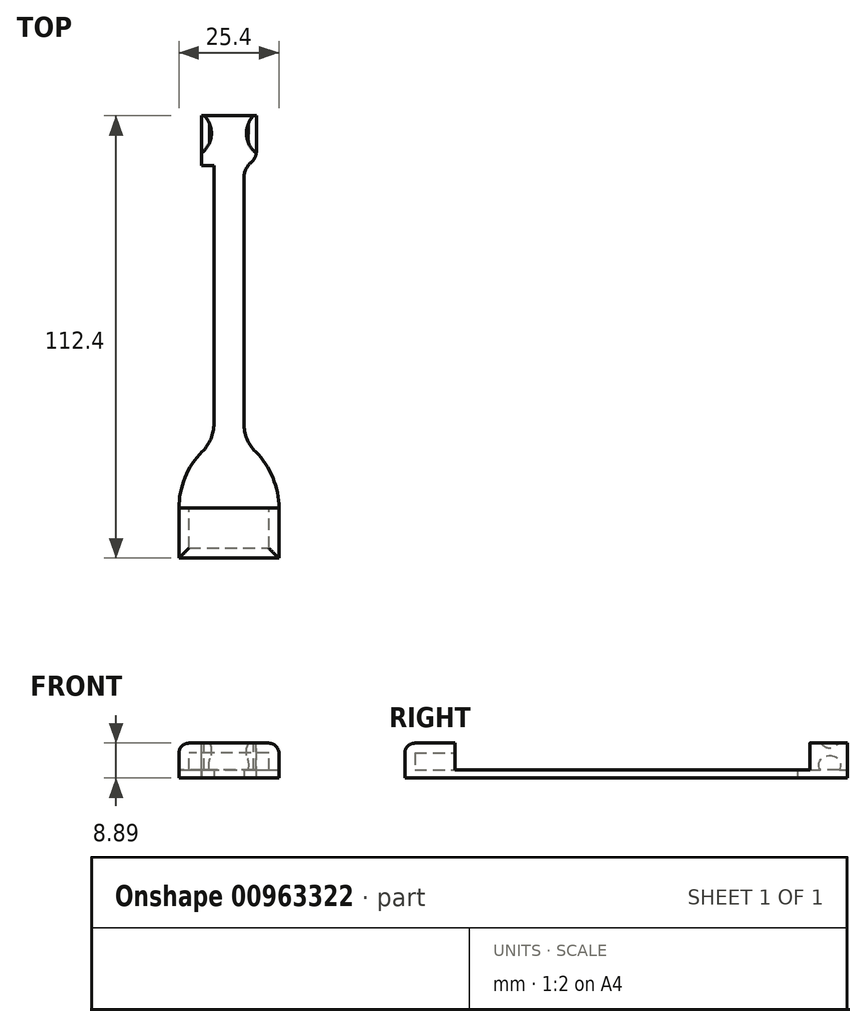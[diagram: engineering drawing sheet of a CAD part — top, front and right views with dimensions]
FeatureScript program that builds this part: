
annotation { "Feature Type Name" : "Feature", "Feature Type Description" : "" }
export const myFeature = defineFeature(function(context is Context, id is Id, definition is map)
    precondition{}
    {
        {
            var Q0;
            Q0=qCreatedBy(makeId("Top.planeOp"),FACE);
            var sketch = newSketch(context, id + "F0", { "sketchPlane" : qUnion([Q0])});
            skLineSegment(sketch, "E0.bottom", {"start": v(0, 0) * mm, "end": v(25.4, 0) * mm});
            skLineSegment(sketch, "E0.top", {"start": v(0, 12.7) * mm, "end": v(25.4, 12.7) * mm});
            skLineSegment(sketch, "E0.left", {"start": v(0, 0) * mm, "end": v(0, 12.7) * mm});
            skLineSegment(sketch, "E0.right", {"start": v(25.4, 0) * mm, "end": v(25.4, 12.7) * mm});
            skSolve(sketch);
        }
        {
            var Q0;
            Q0=makeQuery(id+"F0.imprint","IMPRINT",FACE,{"disambiguationData":[TD([[makeQuery(id+"F0.imprint","IMPRINT",EDGE,{"derivedFrom":sQuery(id+"F0.wireOp",EDGE,"E0.bottom")}),1.0]])]});
            var Q1;
            {var subQ0=sQuery(id+"F0.wireOp",EDGE,"zsi7gBfR-j4X2-UrOj-o1LC-GleYWkfHhouP");Q1=makeQuery(id+"F0.imprint","IMPRINT",FACE,{"disambiguationData":[TD([[makeQuery(id+"F0.imprint","IMPRINT",EDGE,{"derivedFrom":subQ0}),-1.0]])]});}
            extrude(context, id + "F1", {"entities" : qUnion([Q0, Q1]), "depth" : 8.9 * mm, "offsetDistance" : 25.4 * mm});
        }
        {
            var Q0;
            Q0=makeQuery(id+"F1.opExtrude","SWEPT_FACE",FACE,{"disambiguationData":[OSD([sQuery(id+"F0.wireOp",EDGE,"E0.top")])]});
            var sketch = newSketch(context, id + "F2", { "sketchPlane" : qUnion([Q0])});
            skLineSegment(sketch, "E1.bottom", {"start": v(-22.86, 2.03) * mm, "end": v(-2.54, 2.03) * mm});
            skLineSegment(sketch, "E1.top", {"start": v(-22.86, 6.35) * mm, "end": v(-2.54, 6.35) * mm});
            skLineSegment(sketch, "E1.left", {"start": v(-22.86, 2.03) * mm, "end": v(-22.86, 6.35) * mm});
            skLineSegment(sketch, "E1.right", {"start": v(-2.54, 2.03) * mm, "end": v(-2.54, 6.35) * mm});
            skSolve(sketch);
        }
        {
            var Q0;
            Q0=makeQuery(id+"F2.imprint","IMPRINT",FACE,{"disambiguationData":[TD([[makeQuery(id+"F2.imprint","IMPRINT",EDGE,{"derivedFrom":sQuery(id+"F2.wireOp",EDGE,"E1.bottom")}),1.0]])]});
            extrude(context, id + "F3", {"entities" : qUnion([Q0]), "operationType" : NewBodyOperationType.REMOVE, "endBound" : BoundingType.UP_TO_NEXT, "oppositeDirection" : true, "depth" : 9.14 * mm, "hasOffset" : true, "offsetDistance" : 2.54 * mm});
        }
        {
            var Q0;
            Q0=makeQuery(id+"F1.opExtrude","CAP_FACE",FACE,{"disambiguationData":[OSD([sQuery(id+"F0.wireOp",EDGE,"E0.bottom"),sQuery(id+"F0.wireOp",EDGE,"E0.top"),sQuery(id+"F0.wireOp",EDGE,"E0.left"),sQuery(id+"F0.wireOp",EDGE,"E0.right")])],"isStart":true});
            var sketch = newSketch(context, id + "F4", { "sketchPlane" : qUnion([Q0])});
            skArc(sketch, "E2", {"start": v(19.47, -27.04) * mm, "mid": v(23.86, -20.46) * mm, "end": v(25.4, -12.7) * mm});
            skArc(sketch, "E3", {"start": v(19.47, -27.04) * mm, "mid": v(17.28, -30.34) * mm, "end": v(16.51, -34.22) * mm});
            skLineSegment(sketch, "E4", {"start": v(16.51, -34.22) * mm, "end": v(16.51, -99.7) * mm});
            skLineSegment(sketch, "E5", {"start": v(12.7, 0) * mm, "end": v(12.7, -175.53) * mm, "construction": true});
            skLineSegment(sketch, "E6", {"start": v(12.7, -140.95) * mm, "end": v(12.7, -12.7) * mm});
            skLineSegment(sketch, "E7", {"start": v(12.7, -12.7) * mm, "end": v(25.4, -12.7) * mm});
            skLineSegment(sketch, "E8.0.0", {"start": v(2.54, -2.54) * mm, "end": v(22.86, -2.54) * mm});
            skLineSegment(sketch, "E8.0.2", {"start": v(22.86, -2.54) * mm, "end": v(2.54, -2.54) * mm});
            skLineSegment(sketch, "E9", {"start": v(16.51, -99.7) * mm, "end": v(22.86, -99.7) * mm});
            skLineSegment(sketch, "E10", {"start": v(22.86, -99.7) * mm, "end": v(22.86, -112.4) * mm});
            skLineSegment(sketch, "E11", {"start": v(22.86, -112.4) * mm, "end": v(12.7, -112.4) * mm});
            skSolve(sketch);
        }
        {
            var Q0;
            Q0=makeQuery(id+"F4.imprint","IMPRINT",FACE,{"disambiguationData":[TD([[makeQuery(id+"F4.imprint","IMPRINT",EDGE,{"derivedFrom":sQuery(id+"F4.wireOp",EDGE,"E2")}),1.0]])]});
            var Q1;
            Q1=makeQuery(id+"F3.boolean.opBoolean","COPY",FACE,{"derivedFrom":makeQuery(id+"F3.opExtrude","SWEPT_FACE",FACE,{"disambiguationData":[OSD([sQuery(id+"F2.wireOp",EDGE,"E1.bottom")])]})});
            extrude(context, id + "F5", {"entities" : qUnion([Q0]), "endBound" : BoundingType.UP_TO_SURFACE, "oppositeDirection" : true, "depth" : 25.4 * mm, "endBoundEntityFace" : qUnion([Q1]), "offsetDistance" : 25.4 * mm});
        }
        {
            var Q0;
            Q0=makeQuery(id+"F5.opExtrude","SWEPT_BODY",BODY,{"disambiguationData":[OSD([sQuery(id+"F4.wireOp",EDGE,"E2"),sQuery(id+"F4.wireOp",EDGE,"E3"),sQuery(id+"F4.wireOp",EDGE,"E4"),sQuery(id+"F4.wireOp",EDGE,"qD1EN0Aj-AqS1-obng-q8K4-HIYZGEm6BOBV"),sQuery(id+"F4.wireOp",EDGE,"E6"),sQuery(id+"F4.wireOp",EDGE,"E7")])]});
            var Q1;
            Q1=makeQuery(id+"F5.opExtrude","SWEPT_FACE",FACE,{"disambiguationData":[OSD([sQuery(id+"F4.wireOp",EDGE,"E6")])]});
            mirror(context, id + "F6", {"entities" : qUnion([Q0]), "mirrorPlane" : qUnion([Q1])});
        }
        {
            var Q0;
            Q0=makeQuery(id+"F1.opExtrude","SWEPT_BODY",BODY,{"disambiguationData":[OSD([sQuery(id+"F0.wireOp",EDGE,"E0.bottom"),sQuery(id+"F0.wireOp",EDGE,"E0.top"),sQuery(id+"F0.wireOp",EDGE,"E0.left"),sQuery(id+"F0.wireOp",EDGE,"E0.right")])]});
            var Q1;
            Q1=makeQuery(id+"F6.opPattern","COPY",BODY,{"derivedFrom":makeQuery(id+"F5.opExtrude","SWEPT_BODY",BODY,{"disambiguationData":[OSD([sQuery(id+"F4.wireOp",EDGE,"E2"),sQuery(id+"F4.wireOp",EDGE,"E3"),sQuery(id+"F4.wireOp",EDGE,"E4"),sQuery(id+"F4.wireOp",EDGE,"qD1EN0Aj-AqS1-obng-q8K4-HIYZGEm6BOBV"),sQuery(id+"F4.wireOp",EDGE,"E6"),sQuery(id+"F4.wireOp",EDGE,"E7")])]}),"instanceName":"1"});
            var Q2;
            Q2=makeQuery(id+"F5.opExtrude","SWEPT_BODY",BODY,{"disambiguationData":[OSD([sQuery(id+"F4.wireOp",EDGE,"E2"),sQuery(id+"F4.wireOp",EDGE,"E3"),sQuery(id+"F4.wireOp",EDGE,"E4"),sQuery(id+"F4.wireOp",EDGE,"qD1EN0Aj-AqS1-obng-q8K4-HIYZGEm6BOBV"),sQuery(id+"F4.wireOp",EDGE,"E6"),sQuery(id+"F4.wireOp",EDGE,"E7")])]});
            booleanBodies(context, id + "F7", {"operationType" : BooleanOperationType.UNION, "tools" : qUnion([Q0, Q1, Q2])});
        }
        {
            var Q0;
            {var subQ0=makeQuery(id+"F5.opExtrude","CAP_FACE",FACE,{"disambiguationData":[OSD([sQuery(id+"F4.wireOp",EDGE,"E2"),sQuery(id+"F4.wireOp",EDGE,"E3"),sQuery(id+"F4.wireOp",EDGE,"E4"),sQuery(id+"F4.wireOp",EDGE,"E6"),sQuery(id+"F4.wireOp",EDGE,"E7"),sQuery(id+"F4.wireOp",EDGE,"E9"),sQuery(id+"F4.wireOp",EDGE,"E10"),sQuery(id+"F4.wireOp",EDGE,"E11")])],"isStart":false});Q0=makeQuery(id+"F7.opBoolean","MERGE",FACE,{"derivedFrom":[makeQuery(id+"F3.boolean.opBoolean","COPY",FACE,{"derivedFrom":makeQuery(id+"F3.opExtrude","SWEPT_FACE",FACE,{"disambiguationData":[OSD([sQuery(id+"F2.wireOp",EDGE,"E1.bottom")])]})}),subQ0,makeQuery(id+"F6.opPattern","COPY",FACE,{"derivedFrom":subQ0,"instanceName":"1"})]});}
            var sketch = newSketch(context, id + "F8", { "sketchPlane" : qUnion([Q0])});
            skLineSegment(sketch, "E12.bottom", {"start": v(2.54, 99.7) * mm, "end": v(22.86, 99.7) * mm});
            skLineSegment(sketch, "E12.top", {"start": v(2.54, 112.4) * mm, "end": v(22.86, 112.4) * mm});
            skLineSegment(sketch, "E12.left", {"start": v(2.54, 99.7) * mm, "end": v(2.54, 112.4) * mm});
            skLineSegment(sketch, "E12.right", {"start": v(22.86, 99.7) * mm, "end": v(22.86, 112.4) * mm});
            skSolve(sketch);
        }
        {
            var Q0;
            Q0=makeQuery(id+"F8.imprint","IMPRINT",FACE,{"disambiguationData":[TD([[makeQuery(id+"F8.imprint","IMPRINT",EDGE,{"derivedFrom":sQuery(id+"F8.wireOp",EDGE,"E12.top")}),1.0]])]});
            var Q1;
            Q1=makeQuery(id+"F1.opExtrude","CAP_FACE",FACE,{"disambiguationData":[OSD([sQuery(id+"F0.wireOp",EDGE,"E0.bottom"),sQuery(id+"F0.wireOp",EDGE,"E0.top"),sQuery(id+"F0.wireOp",EDGE,"E0.left"),sQuery(id+"F0.wireOp",EDGE,"E0.right")])],"isStart":false});
            extrude(context, id + "F9", {"entities" : qUnion([Q0]), "operationType" : NewBodyOperationType.ADD, "endBound" : BoundingType.UP_TO_SURFACE, "depth" : 6.1 * mm, "endBoundEntityFace" : qUnion([Q1]), "offsetDistance" : 25.4 * mm});
        }
        {
            var Q0;
            {var subQ0=makeQuery(id+"F5.opExtrude","SWEPT_FACE",FACE,{"disambiguationData":[OSD([sQuery(id+"F4.wireOp",EDGE,"E9")])]});Q0=makeQuery(id+"F9.boolean.opBoolean","MERGE",FACE,{"derivedFrom":[subQ0,makeQuery(id+"F6.opPattern","COPY",FACE,{"derivedFrom":subQ0,"instanceName":"1"}),makeQuery(id+"F9.opExtrude","SWEPT_FACE",FACE,{"disambiguationData":[OSD([sQuery(id+"F8.wireOp",EDGE,"E12.bottom")])]})]});}
            var sketch = newSketch(context, id + "F10", { "sketchPlane" : qUnion([Q0])});
            skArc(sketch, "E13", {"start": v(17.62, 2.03) * mm, "mid": v(12.7, 8.38) * mm, "end": v(7.78, 2.03) * mm});
            skPoint(sketch, "E14.0", {"position": v(12.7, 8.9) * mm});
            skLineSegment(sketch, "E15", {"start": v(7.78, 2.03) * mm, "end": v(17.62, 2.03) * mm});
            skLineSegment(sketch, "E16", {"start": v(17.15, 5.76) * mm, "end": v(17.15, 7.67) * mm});
            skLineSegment(sketch, "E17", {"start": v(22.86, 8.9) * mm, "end": v(19.69, 8.9) * mm});
            skLineSegment(sketch, "E18", {"start": v(19.69, 8.9) * mm, "end": v(19.69, 2.03) * mm});
            skLineSegment(sketch, "E19", {"start": v(22.86, 2.03) * mm, "end": v(22.86, 8.9) * mm});
            skLineSegment(sketch, "E20", {"start": v(17.15, 7.67) * mm, "end": v(17.6, 8.9) * mm});
            skLineSegment(sketch, "E21", {"start": v(17.6, 8.9) * mm, "end": v(19.69, 8.9) * mm});
            skLineSegment(sketch, "E22", {"start": v(17.62, 2.03) * mm, "end": v(19.69, 2.03) * mm});
            skLineSegment(sketch, "E23", {"start": v(12.7, 8.9) * mm, "end": v(12.7, 3.3) * mm, "construction": true});
            skLineSegment(sketch, "E24.MirrorCS", {"start": v(8.26, 5.76) * mm, "end": v(8.26, 7.67) * mm});
            skLineSegment(sketch, "E25.MirrorCS", {"start": v(8.26, 7.67) * mm, "end": v(7.8, 8.9) * mm});
            skLineSegment(sketch, "E26.MirrorCS", {"start": v(7.8, 8.9) * mm, "end": v(5.72, 8.9) * mm});
            skLineSegment(sketch, "E27.MirrorCS", {"start": v(5.72, 8.9) * mm, "end": v(5.72, 2.03) * mm});
            skLineSegment(sketch, "E28.MirrorCS", {"start": v(7.78, 2.03) * mm, "end": v(5.72, 2.03) * mm});
            skLineSegment(sketch, "E29.MirrorCS", {"start": v(2.54, 2.03) * mm, "end": v(2.54, 8.9) * mm});
            skLineSegment(sketch, "E30.MirrorCS", {"start": v(2.54, 8.9) * mm, "end": v(5.72, 8.9) * mm});
            skLineSegment(sketch, "E31", {"start": v(22.86, 2.03) * mm, "end": v(22.86, 0) * mm});
            skLineSegment(sketch, "E32", {"start": v(22.86, 0) * mm, "end": v(19.69, 0) * mm});
            skLineSegment(sketch, "E33", {"start": v(19.69, 0) * mm, "end": v(19.69, 2.03) * mm});
            skLineSegment(sketch, "E34.MirrorCS", {"start": v(5.72, 0) * mm, "end": v(5.72, 2.03) * mm});
            skLineSegment(sketch, "E35.MirrorCS", {"start": v(2.54, 0) * mm, "end": v(5.72, 0) * mm});
            skLineSegment(sketch, "E36.MirrorCS", {"start": v(2.54, 2.03) * mm, "end": v(2.54, 0) * mm});
            skSolve(sketch);
        }
        {
            var Q0;
            {var subQ2=sQuery(id+"F10.wireOp",EDGE,"E16");Q0=makeQuery(id+"F10.imprint","IMPRINT",FACE,{"disambiguationData":[TD([[makeQuery(id+"F10.imprint","IMPRINT",EDGE,{"derivedFrom":subQ2}),1.0]])]});}
            var Q1;
            {var subQ0=sQuery(id+"F10.wireOp",EDGE,"E15");Q1=makeQuery(id+"F10.imprint","IMPRINT",FACE,{"disambiguationData":[TD([[makeQuery(id+"F10.imprint","IMPRINT",EDGE,{"derivedFrom":subQ0}),1.0]])]});}
            var Q2;
            Q2=makeQuery(id+"F10.imprint","IMPRINT",FACE,{"disambiguationData":[TD([[makeQuery(id+"F10.imprint","IMPRINT",EDGE,{"derivedFrom":sQuery(id+"F10.wireOp",EDGE,"E17")}),-1.0]])]});
            var Q3;
            Q3=makeQuery(id+"F10.imprint","IMPRINT",FACE,{"disambiguationData":[TD([[makeQuery(id+"F10.imprint","IMPRINT",EDGE,{"derivedFrom":sQuery(id+"F10.wireOp",EDGE,"E27.MirrorCS")}),-1.0]])]});
            extrude(context, id + "F11", {"entities" : qUnion([Q0, Q1, Q2, Q3]), "operationType" : NewBodyOperationType.REMOVE, "endBound" : BoundingType.UP_TO_NEXT, "oppositeDirection" : true, "depth" : 25.4 * mm, "offsetDistance" : 25.4 * mm});
        }
        {
            var Q0;
            {var subQ2=sQuery(id+"F8.wireOp",EDGE,"E12.bottom");var subQ3=sQuery(id+"F8.wireOp",EDGE,"E12.top");Q0=makeQuery(id+"F11.boolean.opBoolean","SPLIT",FACE,{"disambiguationData":[TD([makeQuery(id+"F11.opExtrude","SWEPT_FACE",FACE,{"disambiguationData":[OSD([sQuery(id+"F10.wireOp",EDGE,"E20")])]})])],"derivedFrom":makeQuery(id+"F9.opExtrude","CAP_FACE",FACE,{"disambiguationData":[OSD([subQ2,subQ3,sQuery(id+"F8.wireOp",EDGE,"E12.left"),sQuery(id+"F8.wireOp",EDGE,"E12.right")])],"isStart":false})});}
            var sketch = newSketch(context, id + "F12", { "sketchPlane" : qUnion([Q0])});
            skPoint(sketch, "E37.0", {"position": v(12.7, 112.4) * mm});
            skLineSegment(sketch, "E38", {"start": v(12.7, 112.4) * mm, "end": v(12.7, 92) * mm, "construction": true});
            skCircle(sketch, "E39", {"center": v(23.5, 107.95) * mm, "radius": 6.35 * mm});
            skLineSegment(sketch, "E40", {"start": v(19.69, 99.7) * mm, "end": v(19.69, 102.87) * mm});
            skLineSegment(sketch, "E41", {"start": v(19.69, 112.4) * mm, "end": v(17.15, 112.4) * mm});
            skPoint(sketch, "E41.endSnap0", {"position": v(18.64, 112.4) * mm});
            skLineSegment(sketch, "E42", {"start": v(17.15, 112.4) * mm, "end": v(17.15, 99.7) * mm});
            skLineSegment(sketch, "E43", {"start": v(17.15, 99.7) * mm, "end": v(19.69, 99.7) * mm});
            skLineSegment(sketch, "E44.MirrorCS", {"start": v(8.26, 112.4) * mm, "end": v(8.26, 99.7) * mm});
            skCircle(sketch, "E45.MirrorC", {"center": v(1.9, 107.95) * mm, "radius": 6.35 * mm});
            skLineSegment(sketch, "E46.MirrorCS", {"start": v(5.72, 99.7) * mm, "end": v(5.72, 102.87) * mm});
            skLineSegment(sketch, "E47.MirrorCS", {"start": v(8.26, 99.7) * mm, "end": v(5.72, 99.7) * mm});
            skLineSegment(sketch, "E48.MirrorCS", {"start": v(5.72, 112.4) * mm, "end": v(8.26, 112.4) * mm});
            skSolve(sketch);
        }
        {
            var Q0;
            {var subQ0=sQuery(id+"F12.wireOp",EDGE,"E40");Q0=makeQuery(id+"F12.imprint","IMPRINT",FACE,{"disambiguationData":[TD([[makeQuery(id+"F12.imprint","IMPRINT",EDGE,{"derivedFrom":subQ0}),-1.0]])]});}
            var Q1;
            {var subQ0=sQuery(id+"F12.wireOp",EDGE,"E42");var subQ5=sQuery(id+"F12.wireOp",EDGE,"E43");var subQ7=makeQuery(id+"F12.imprint","INTERSECT",VERTEX,{"derivedFrom":[subQ0,subQ5]});Q1=makeQuery(id+"F12.imprint","IMPRINT",FACE,{"disambiguationData":[TD([[makeQuery(id+"F12.imprint","IMPRINT",EDGE,{"disambiguationData":[TD([[subQ7,1.0]])],"derivedFrom":subQ0}),1.0]])]});}
            var Q2;
            {var subQ0=sQuery(id+"F12.wireOp",EDGE,"E42");var subQ1=sQuery(id+"F12.wireOp",EDGE,"E39");var subQ2=makeQuery(id+"F12.imprint","INTERSECT",VERTEX,{"derivedFrom":[subQ1,subQ0]});Q2=makeQuery(id+"F12.imprint","IMPRINT",FACE,{"disambiguationData":[TD([[makeQuery(id+"F12.imprint","IMPRINT",EDGE,{"disambiguationData":[TD([[subQ2,1.0]])],"derivedFrom":subQ1}),-1.0]])]});}
            var Q3;
            {var subQ4=sQuery(id+"F12.wireOp",EDGE,"E46.MirrorCS");Q3=makeQuery(id+"F12.imprint","IMPRINT",FACE,{"disambiguationData":[TD([[makeQuery(id+"F12.imprint","IMPRINT",EDGE,{"derivedFrom":subQ4}),-1.0]])]});}
            var Q4;
            {var subQ0=sQuery(id+"F12.wireOp",EDGE,"E48.MirrorCS");var subQ1=sQuery(id+"F12.wireOp",EDGE,"E44.MirrorCS");var subQ2=makeQuery(id+"F12.imprint","INTERSECT",VERTEX,{"derivedFrom":[subQ1,subQ0]});Q4=makeQuery(id+"F12.imprint","IMPRINT",FACE,{"disambiguationData":[TD([[makeQuery(id+"F12.imprint","IMPRINT",EDGE,{"disambiguationData":[TD([[subQ2,-1.0]])],"derivedFrom":subQ1}),-1.0]])]});}
            var Q5;
            {var subQ0=sQuery(id+"F12.wireOp",EDGE,"E41");var subQ1=sQuery(id+"F12.wireOp",EDGE,"E39");var subQ2=makeQuery(id+"F12.imprint","INTERSECT",VERTEX,{"derivedFrom":[subQ1,subQ0]});Q5=makeQuery(id+"F12.imprint","IMPRINT",FACE,{"disambiguationData":[TD([[makeQuery(id+"F12.imprint","IMPRINT",EDGE,{"disambiguationData":[TD([[subQ2,-1.0]])],"derivedFrom":subQ1}),-1.0]])]});}
            var Q6;
            {var subQ0=makeQuery(id+"F5.opExtrude","CAP_FACE",FACE,{"disambiguationData":[OSD([sQuery(id+"F4.wireOp",EDGE,"E2"),sQuery(id+"F4.wireOp",EDGE,"E3"),sQuery(id+"F4.wireOp",EDGE,"E4"),sQuery(id+"F4.wireOp",EDGE,"E6"),sQuery(id+"F4.wireOp",EDGE,"E7"),sQuery(id+"F4.wireOp",EDGE,"E9"),sQuery(id+"F4.wireOp",EDGE,"E10"),sQuery(id+"F4.wireOp",EDGE,"E11")])],"isStart":false});Q6=makeQuery(id+"F11.boolean.opBoolean","MERGE",FACE,{"derivedFrom":[makeQuery(id+"F7.opBoolean","MERGE",FACE,{"derivedFrom":[makeQuery(id+"F3.boolean.opBoolean","COPY",FACE,{"derivedFrom":makeQuery(id+"F3.opExtrude","SWEPT_FACE",FACE,{"disambiguationData":[OSD([sQuery(id+"F2.wireOp",EDGE,"E1.bottom")])]})}),subQ0,makeQuery(id+"F6.opPattern","COPY",FACE,{"derivedFrom":subQ0,"instanceName":"1"})]})],"fromTools":[makeQuery(id+"F11.opExtrude","SWEPT_FACE",FACE,{"disambiguationData":[OSD([sQuery(id+"F10.wireOp",EDGE,"E15")])]})]});}
            extrude(context, id + "F13", {"entities" : qUnion([Q0, Q1, Q2, Q3, Q4, Q5]), "operationType" : NewBodyOperationType.REMOVE, "endBound" : BoundingType.UP_TO_SURFACE, "oppositeDirection" : true, "depth" : 25.4 * mm, "endBoundEntityFace" : qUnion([Q6]), "offsetDistance" : 25.4 * mm});
        }
        {
            var Q0;
            Q0=makeQuery(id+"F11.boolean.opBoolean","COPY",EDGE,{"derivedFrom":makeQuery(id+"F11.opExtrude","CAP_EDGE",EDGE,{"disambiguationData":[OSD([sQuery(id+"F10.wireOp",EDGE,"E18"),sQuery(id+"F10.wireOp",EDGE,"E33")])],"isStart":true})});
            var Q1;
            Q1=makeQuery(id+"F11.boolean.opBoolean","COPY",EDGE,{"derivedFrom":makeQuery(id+"F11.opExtrude","CAP_EDGE",EDGE,{"disambiguationData":[OSD([sQuery(id+"F10.wireOp",EDGE,"E27.MirrorCS"),sQuery(id+"F10.wireOp",EDGE,"E34.MirrorCS")])],"isStart":true})});
            var Q2;
            Q2=makeQuery(id+"F11.boolean.opBoolean","COPY",EDGE,{"derivedFrom":makeQuery(id+"F11.opExtrude","CAP_EDGE",EDGE,{"disambiguationData":[OSD([sQuery(id+"F10.wireOp",EDGE,"E27.MirrorCS"),sQuery(id+"F10.wireOp",EDGE,"E34.MirrorCS")])],"isStart":false})});
            var Q3;
            Q3=makeQuery(id+"F11.boolean.opBoolean","COPY",EDGE,{"derivedFrom":makeQuery(id+"F11.opExtrude","CAP_EDGE",EDGE,{"disambiguationData":[OSD([sQuery(id+"F10.wireOp",EDGE,"E18"),sQuery(id+"F10.wireOp",EDGE,"E33")])],"isStart":false})});
            fillet(context, id + "F14", {"entities" : qUnion([Q0, Q1, Q2, Q3]), "radius" : 3.8 * mm, "tangentPropagation" : true, "allowEdgeOverflow" : false});
        }
        {
            var Q0;
            Q0=makeQuery(id+"F14.opFillet","BLEND_EDGE",EDGE,{"blendedFrom":[makeQuery(id+"F11.boolean.opBoolean","COPY",EDGE,{"derivedFrom":makeQuery(id+"F11.opExtrude","CAP_EDGE",EDGE,{"disambiguationData":[OSD([sQuery(id+"F10.wireOp",EDGE,"E18"),sQuery(id+"F10.wireOp",EDGE,"E33")])],"isStart":true})}),makeQuery(id+"F5.opExtrude","SWEPT_FACE",FACE,{"disambiguationData":[OSD([sQuery(id+"F4.wireOp",EDGE,"E4")])]})],"blendedInto":[makeQuery(id+"F5.opExtrude","SWEPT_FACE",FACE,{"disambiguationData":[OSD([sQuery(id+"F4.wireOp",EDGE,"E4")])]})]});
            var Q1;
            Q1=makeQuery(id+"F14.opFillet","BLEND_EDGE",EDGE,{"blendedFrom":[makeQuery(id+"F11.boolean.opBoolean","COPY",EDGE,{"derivedFrom":makeQuery(id+"F11.opExtrude","CAP_EDGE",EDGE,{"disambiguationData":[OSD([sQuery(id+"F10.wireOp",EDGE,"E27.MirrorCS"),sQuery(id+"F10.wireOp",EDGE,"E34.MirrorCS")])],"isStart":true})}),makeQuery(id+"F6.opPattern","COPY",FACE,{"derivedFrom":makeQuery(id+"F5.opExtrude","SWEPT_FACE",FACE,{"disambiguationData":[OSD([sQuery(id+"F4.wireOp",EDGE,"E4")])]}),"instanceName":"1"})],"blendedInto":[makeQuery(id+"F6.opPattern","COPY",FACE,{"derivedFrom":makeQuery(id+"F5.opExtrude","SWEPT_FACE",FACE,{"disambiguationData":[OSD([sQuery(id+"F4.wireOp",EDGE,"E4")])]}),"instanceName":"1"})]});
            fillet(context, id + "F15", {"entities" : qUnion([Q0, Q1]), "radius" : 5.08 * mm, "tangentPropagation" : true, "allowEdgeOverflow" : false});
        }
        {
            var Q0;
            Q0=makeQuery(id+"F1.opExtrude","CAP_EDGE",EDGE,{"disambiguationData":[OSD([sQuery(id+"F0.wireOp",EDGE,"E0.right")])],"isStart":false});
            var Q1;
            Q1=makeQuery(id+"F1.opExtrude","CAP_EDGE",EDGE,{"disambiguationData":[OSD([sQuery(id+"F0.wireOp",EDGE,"E0.bottom")])],"isStart":false});
            var Q2;
            Q2=makeQuery(id+"F1.opExtrude","CAP_EDGE",EDGE,{"disambiguationData":[OSD([sQuery(id+"F0.wireOp",EDGE,"E0.left")])],"isStart":false});
            fillet(context, id + "F16", {"entities" : qUnion([Q0, Q1, Q2]), "radius" : 2.54 * mm, "tangentPropagation" : true, "allowEdgeOverflow" : false});
        }
    });
